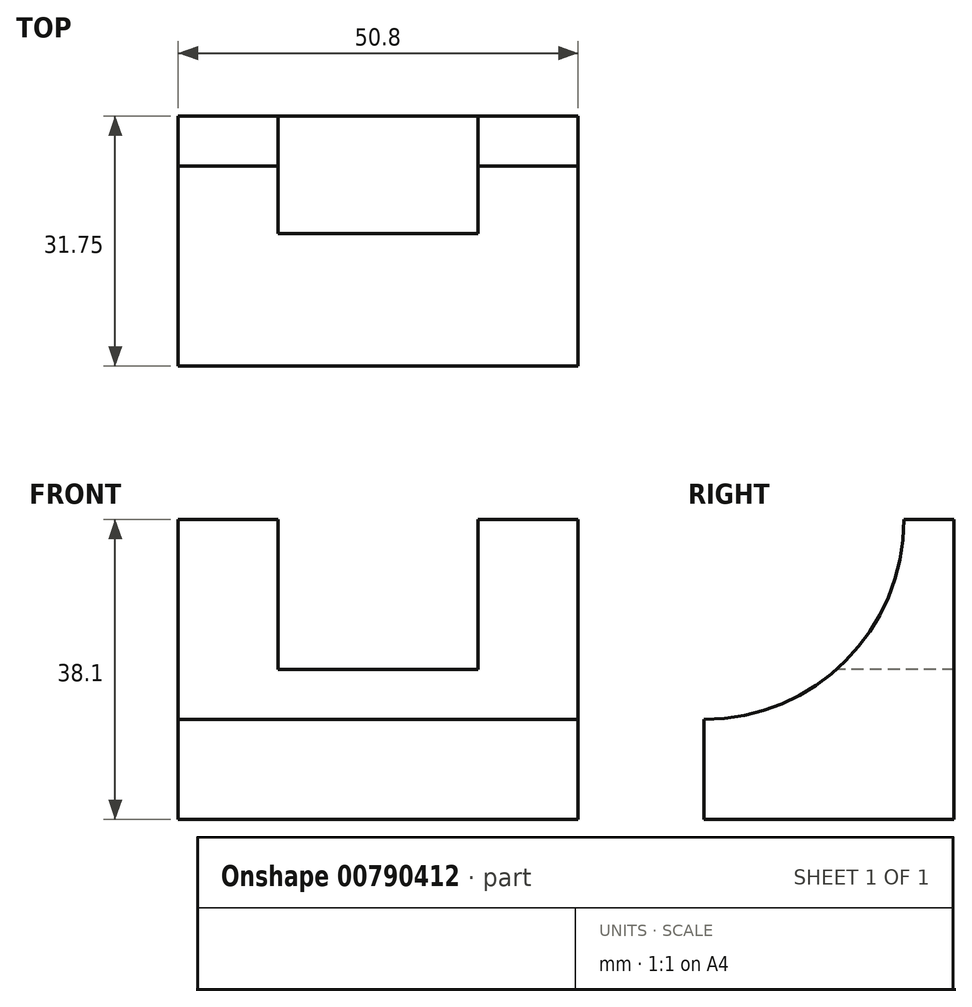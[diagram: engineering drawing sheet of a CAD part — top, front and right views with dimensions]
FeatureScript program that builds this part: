
annotation { "Feature Type Name" : "Feature", "Feature Type Description" : "" }
export const myFeature = defineFeature(function(context is Context, id is Id, definition is map)
    precondition{}
    {
        {
            var Q0;
            Q0=qCreatedBy(makeId("Right.planeOp"),FACE);
            var sketch = newSketch(context, id + "F0", { "sketchPlane" : qUnion([Q0])});
            skLineSegment(sketch, "E0.bottom", {"start": v(0, 0) * mm, "end": v(-31.75, 0) * mm});
            skLineSegment(sketch, "E0.top", {"start": v(0, 38.1) * mm, "end": v(-31.75, 38.1) * mm});
            skLineSegment(sketch, "E0.left", {"start": v(0, 0) * mm, "end": v(0, 38.1) * mm});
            skLineSegment(sketch, "E0.right", {"start": v(-31.75, 0) * mm, "end": v(-31.75, 38.1) * mm});
            skSolve(sketch);
        }
        {
            var Q0;
            Q0=qSketchRegion(id+"F0",true);
            extrude(context, id + "F1", {"entities" : qUnion([Q0]), "depth" : 50.8 * mm, "offsetDistance" : 25.4 * mm});
        }
        {
            var Q0;
            Q0=makeQuery(id+"F1.opExtrude","SWEPT_FACE",FACE,{"disambiguationData":[OSD([sQuery(id+"F0.wireOp",EDGE,"E0.right")])]});
            var sketch = newSketch(context, id + "F2", { "sketchPlane" : qUnion([Q0])});
            skLineSegment(sketch, "E1.bottom", {"start": v(12.7, 38.1) * mm, "end": v(38.1, 38.1) * mm});
            skLineSegment(sketch, "E1.top", {"start": v(12.7, 19.05) * mm, "end": v(38.1, 19.05) * mm});
            skLineSegment(sketch, "E1.left", {"start": v(12.7, 38.1) * mm, "end": v(12.7, 19.05) * mm});
            skLineSegment(sketch, "E1.right", {"start": v(38.1, 38.1) * mm, "end": v(38.1, 19.05) * mm});
            skSolve(sketch);
        }
        {
            var Q0;
            Q0=makeQuery(id+"F2.imprint","IMPRINT",FACE,{"disambiguationData":[TD([[makeQuery(id+"F2.imprint","IMPRINT",EDGE,{"derivedFrom":sQuery(id+"F2.wireOp",EDGE,"E1.bottom")}),1.0]])]});
            extrude(context, id + "F3", {"entities" : qUnion([Q0]), "operationType" : NewBodyOperationType.REMOVE, "oppositeDirection" : true, "depth" : 31.75 * mm, "offsetDistance" : 25.4 * mm});
        }
        {
            var Q0;
            Q0=makeQuery(id+"F1.opExtrude","CAP_FACE",FACE,{"disambiguationData":[OSD([sQuery(id+"F0.wireOp",EDGE,"E0.bottom"),sQuery(id+"F0.wireOp",EDGE,"E0.top"),sQuery(id+"F0.wireOp",EDGE,"E0.left"),sQuery(id+"F0.wireOp",EDGE,"E0.right")])],"isStart":false});
            var sketch = newSketch(context, id + "F4", { "sketchPlane" : qUnion([Q0])});
            skCircle(sketch, "E2", {"center": v(-31.75, 38.1) * mm, "radius": 25.4 * mm});
            skSolve(sketch);
        }
        {
            var Q0;
            Q0=qSketchRegion(id+"F4",true);
            extrude(context, id + "F5", {"entities" : qUnion([Q0]), "operationType" : NewBodyOperationType.REMOVE, "oppositeDirection" : true, "depth" : 50.8 * mm, "offsetDistance" : 25.4 * mm});
        }
    });
